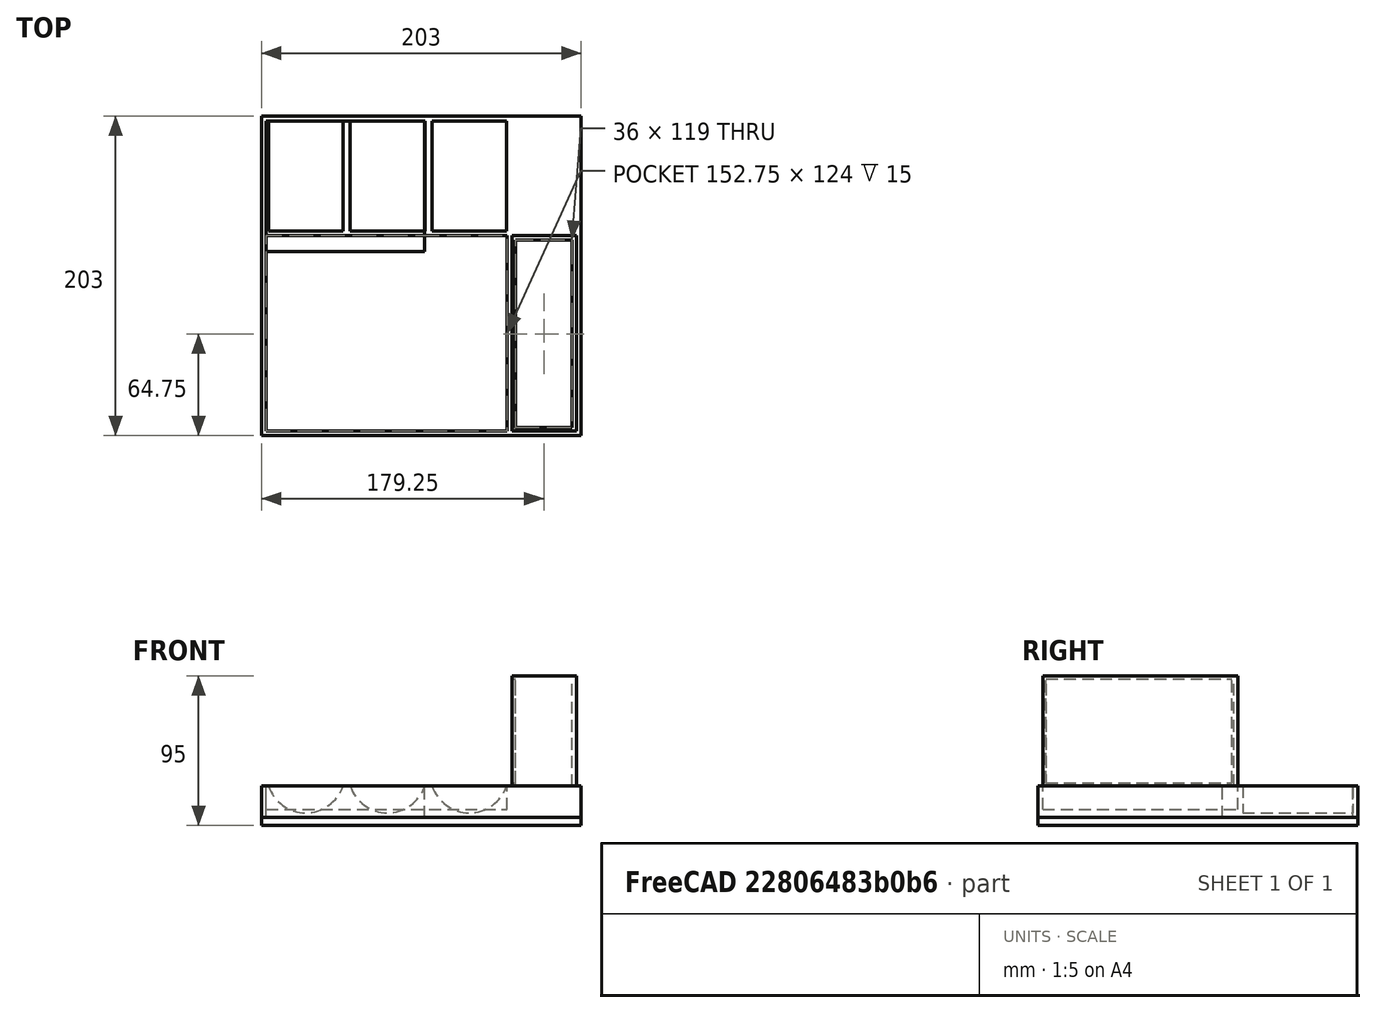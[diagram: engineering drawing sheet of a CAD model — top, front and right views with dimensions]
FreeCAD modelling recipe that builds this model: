
FCSTD DOCUMENT  (FreeCAD 1.0RUnknown)
Label: desk-storage
License: All rights reserved
LicenseURL: https://en.wikipedia.org/wiki/All_rights_reserved
objects: Part::Box×7, Part::Cut×5, Part::Cylinder×3
note: 15 computed .brp shape members not serialized (recipe doc carries the construction recipe); baked Part::Feature solids carry a one-line shape summary decoded from their .brp

FEATURE [Part::Box] Box  label="Cube"
  AttacherType = Attacher::AttachEngine3D
  Height = 5
  Length = 203
  Width = 203
FEATURE [Part::Box] Box001  label="Cube001"
  AttacherType = Attacher::AttachEngine3D
  Height = 20
  Length = 203
  Placement = pos=(0,0,5) rot=(0,0,1;0rad)
  Width = 203
FEATURE [Part::Box] Box002  label="Cube002"
  AttacherType = Attacher::AttachEngine3D
  Height = 20
  Length = 152.75
  Placement = pos=(3,3,10) rot=(0,0,1;0rad)
  Width = 124
FEATURE [Part::Box] Box003  label="Cube003"
  AttacherType = Attacher::AttachEngine3D
  Height = 20
  Length = 100.5
  Placement = pos=(3,117,5) rot=(0,0,1;0rad)
  Width = 83
FEATURE [Part::Cylinder] Cylinder
  Angle = 360
  AttacherType = Attacher::AttachEngine3D
  FirstAngle = 0
  Height = 70
  Placement = pos=(28,200,33) rot=(1,0,0;1.5708rad)
  Radius = 25
  SecondAngle = 0
FEATURE [Part::Cylinder] Cylinder001
  Angle = 360
  AttacherType = Attacher::AttachEngine3D
  FirstAngle = 0
  Height = 70
  Placement = pos=(80,200,33) rot=(1,0,0;1.5708rad)
  Radius = 25
  SecondAngle = 0
FEATURE [Part::Cut] Cut
  Base = -> Box001
  Tool = -> Cylinder
FEATURE [Part::Cylinder] Cylinder002
  Angle = 360
  AttacherType = Attacher::AttachEngine3D
  FirstAngle = 0
  Height = 70
  Placement = pos=(132,200,33) rot=(1,0,0;1.5708rad)
  Radius = 25
  SecondAngle = 0
FEATURE [Part::Cut] Cut001
  Base = -> Cut
  Tool = -> Cylinder001
FEATURE [Part::Cut] Cut002
  Base = -> Cut001
  Tool = -> Cylinder002
FEATURE [Part::Box] Box004  label="Cube004"
  AttacherType = Attacher::AttachEngine3D
  Height = 70
  Length = 41
  Placement = pos=(159,3,25) rot=(0,0,1;0rad)
  Width = 124
FEATURE [Part::Box] Box005  label="Cube005"
  AttacherType = Attacher::AttachEngine3D
  Height = 92
  Length = 36
  Placement = pos=(161.25,5.25,8) rot=(0,0,1;0rad)
  Width = 119
FEATURE [Part::Cut] Cut003
  Base = -> Box004
  Tool = -> Box005
FEATURE [Part::Cut] Cut004
  Base = -> Cut002
  Tool = -> Box002
FEATURE [Part::Box] Box006  label="Cube006"
  AttacherType = Attacher::AttachEngine3D
  Height = 66
  Length = 2.25
  Placement = pos=(159,5,27) rot=(0,0,1;0rad)
  Width = 118
